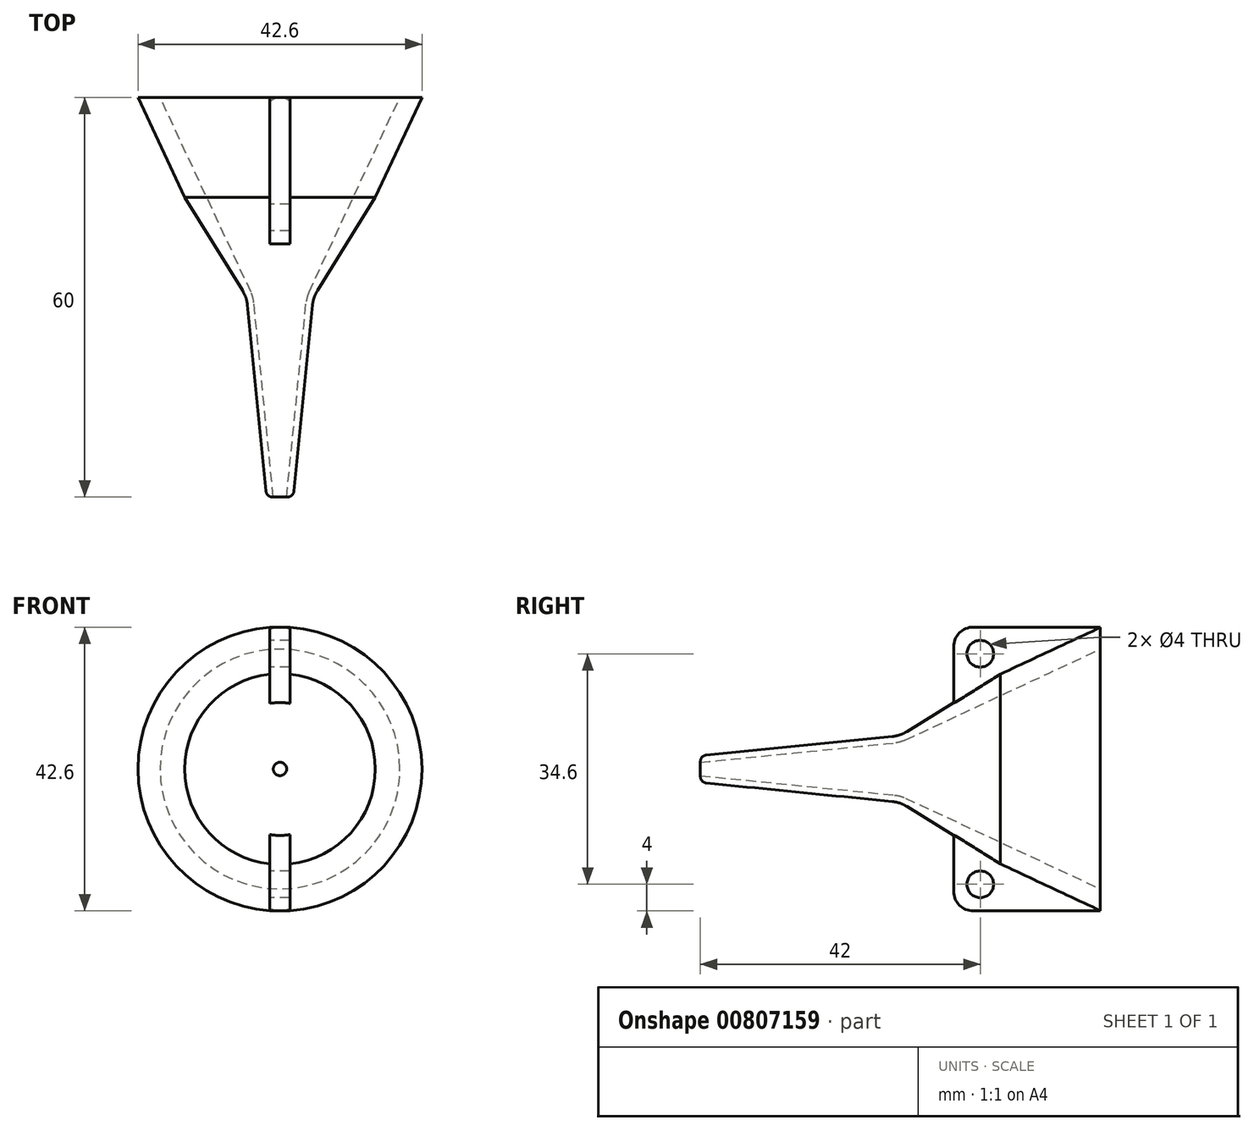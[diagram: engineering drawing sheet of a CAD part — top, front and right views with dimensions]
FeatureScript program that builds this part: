
annotation { "Feature Type Name" : "Feature", "Feature Type Description" : "" }
export const myFeature = defineFeature(function(context is Context, id is Id, definition is map)
    precondition{}
    {
        {
            var Q0;
            Q0=qCreatedBy(makeId("Right.planeOp"),FACE);
            var sketch = newSketch(context, id + "F0", { "sketchPlane" : qUnion([Q0])});
            skLineSegment(sketch, "E0", {"start": v(-30, 1) * mm, "end": v(0, 4) * mm});
            skLineSegment(sketch, "E1", {"start": v(0, 5) * mm, "end": v(-30, 2) * mm});
            skLineSegment(sketch, "E2", {"start": v(-30, 2) * mm, "end": v(-30, 1) * mm});
            skLineSegment(sketch, "E3", {"start": v(32.54, 0) * mm, "end": v(-51.88, 0) * mm, "construction": true});
            skLineSegment(sketch, "E4", {"start": v(0, 5) * mm, "end": v(15, 14.3) * mm});
            skLineSegment(sketch, "E5", {"start": v(0, 4) * mm, "end": v(15, 11) * mm});
            skLineSegment(sketch, "E6", {"start": v(0, 4) * mm, "end": v(20.39, 4) * mm, "construction": true});
            skLineSegment(sketch, "E7", {"start": v(15, 14.3) * mm, "end": v(15, 11) * mm, "construction": true});
            skLineSegment(sketch, "E8", {"start": v(15, 11) * mm, "end": v(30, 17.99) * mm});
            skLineSegment(sketch, "E9", {"start": v(15, 14.3) * mm, "end": v(30, 21.3) * mm});
            skLineSegment(sketch, "E10", {"start": v(30, 21.3) * mm, "end": v(30, 17.99) * mm});
            skSolve(sketch);
        }
        {
            var Q0;
            Q0 = qSketchRegion(id + "F0", true);
            var Q1;
            Q1=sQuery(id+"F0.wireOp",EDGE,"E3");
            revolve(context, id + "F1", {"surfaceOperationType" : NewSurfaceOperationType.NEW, "entities" : qUnion([Q0]), "axis" : qUnion([Q1]), "revolveType" : RevolveType.FULL});
        }
        {
            var Q0;
            Q0=qCreatedBy(makeId("Right.planeOp"),FACE);
            var sketch = newSketch(context, id + "F2", { "sketchPlane" : qUnion([Q0])});
            skLineSegment(sketch, "E11", {"start": v(30, 21.3) * mm, "end": v(8, 21.3) * mm});
            skLineSegment(sketch, "E12", {"start": v(8, 21.3) * mm, "end": v(8, 9.1) * mm});
            skLineSegment(sketch, "E13", {"start": v(8, 9.1) * mm, "end": v(30, 21.3) * mm});
            skCircle(sketch, "E14", {"center": v(12, 17.3) * mm, "radius": 2 * mm});
            skLineSegment(sketch, "E15.MirrorCS", {"start": v(30, -21.3) * mm, "end": v(8, -21.3) * mm});
            skLineSegment(sketch, "E16.MirrorCS", {"start": v(8, -21.3) * mm, "end": v(8, -9.1) * mm});
            skLineSegment(sketch, "E17.MirrorCS", {"start": v(8, -9.1) * mm, "end": v(30, -21.3) * mm});
            skCircle(sketch, "E18.MirrorC", {"center": v(12, -17.3) * mm, "radius": 2 * mm});
            skSolve(sketch);
        }
        {
            var Q0;
            Q0 = qSketchRegion(id + "F2", true);
            extrude(context, id + "F3", {"entities" : qUnion([Q0]), "operationType" : NewBodyOperationType.ADD, "endBound" : BoundingType.SYMMETRIC, "depth" : 3 * mm, "offsetDistance" : 25 * mm});
        }
        {
            var Q0;
            Q0=makeQuery(id+"F1.opRevolve","SWEPT_EDGE",EDGE,{"disambiguationData":[OSD([sQuery(id+"F0.wireOp",EDGE,"E1"),sQuery(id+"F0.wireOp",EDGE,"E2")])]});
            fillet(context, id + "F4", {"entities" : qUnion([Q0]), "radius" : 1 * mm, "tangentPropagation" : true, "allowEdgeOverflow" : false});
        }
        {
            var Q0;
            Q0=makeQuery(id+"F1.opRevolve","SWEPT_EDGE",EDGE,{"disambiguationData":[OSD([sQuery(id+"F0.wireOp",EDGE,"E1"),sQuery(id+"F0.wireOp",EDGE,"E4")])]});
            fillet(context, id + "F5", {"entities" : qUnion([Q0]), "radius" : 5 * mm, "tangentPropagation" : true, "allowEdgeOverflow" : false});
        }
        {
            var Q0;
            Q0=makeQuery(id+"F1.opRevolve","SWEPT_EDGE",EDGE,{"disambiguationData":[OSD([sQuery(id+"F0.wireOp",EDGE,"E0"),sQuery(id+"F0.wireOp",EDGE,"E5")])]});
            fillet(context, id + "F6", {"entities" : qUnion([Q0]), "radius" : 5 * mm, "tangentPropagation" : true, "allowEdgeOverflow" : false});
        }
        {
            var Q0;
            Q0=makeQuery(id+"F3.opExtrude","SWEPT_EDGE",EDGE,{"disambiguationData":[OSD([sQuery(id+"F2.wireOp",EDGE,"E11"),sQuery(id+"F2.wireOp",EDGE,"E12")])]});
            var Q1;
            Q1=makeQuery(id+"F3.opExtrude","SWEPT_EDGE",EDGE,{"disambiguationData":[OSD([sQuery(id+"F2.wireOp",EDGE,"E15.MirrorCS"),sQuery(id+"F2.wireOp",EDGE,"E16.MirrorCS")])]});
            fillet(context, id + "F7", {"entities" : qUnion([Q0, Q1]), "radius" : 3 * mm, "tangentPropagation" : true, "allowEdgeOverflow" : false});
        }
    });
